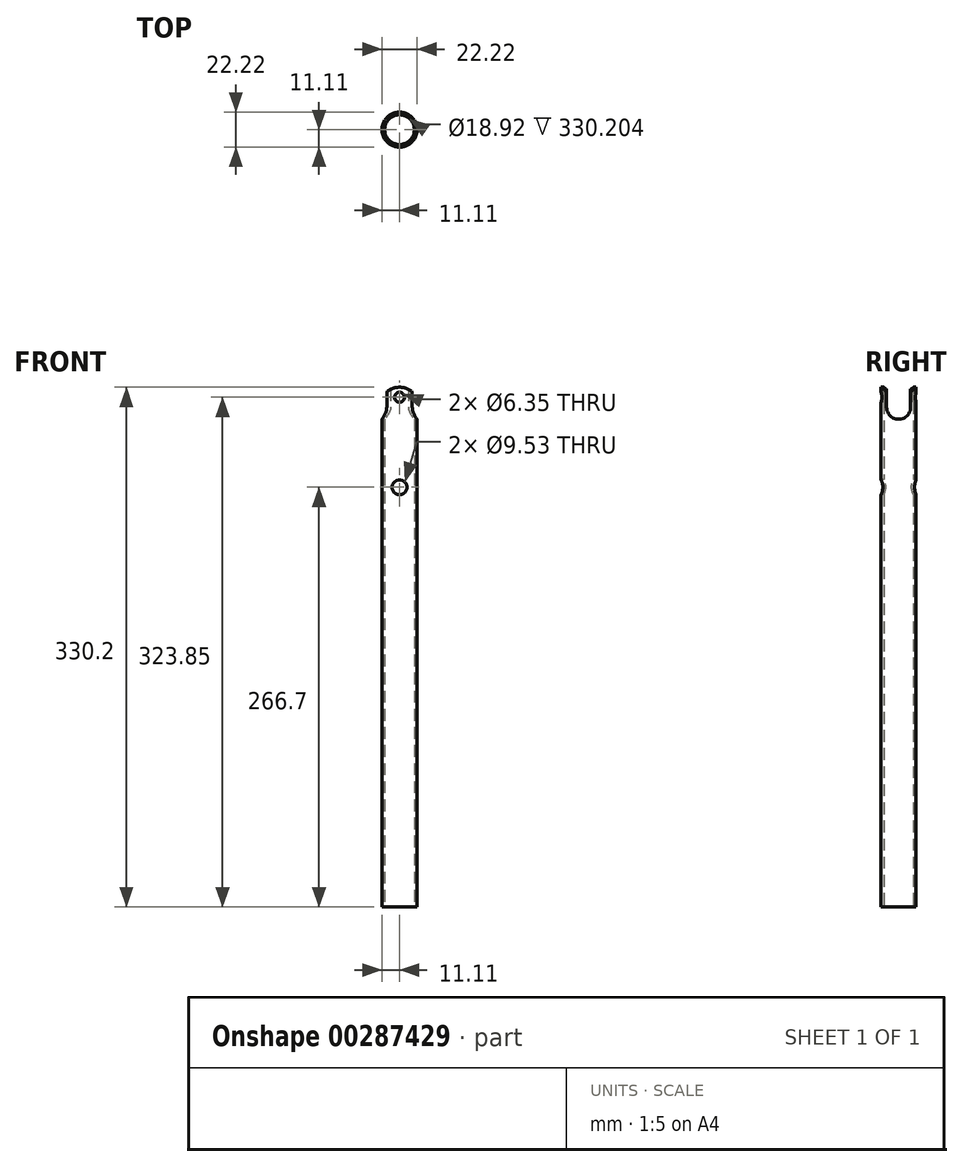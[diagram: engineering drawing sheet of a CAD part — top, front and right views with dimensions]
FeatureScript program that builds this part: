
annotation { "Feature Type Name" : "Feature", "Feature Type Description" : "" }
export const myFeature = defineFeature(function(context is Context, id is Id, definition is map)
    precondition{}
    {
        {
            var Q0;
            Q0=qCreatedBy(makeId("Top.planeOp"),FACE);
            var sketch = newSketch(context, id + "F0", { "sketchPlane" : qUnion([Q0])});
            skCircle(sketch, "E0", {"center": v(0, 0) * mm, "radius": 11.11 * mm});
            skCircle(sketch, "E1", {"center": v(0, 0) * mm, "radius": 9.46 * mm});
            skSolve(sketch);
        }
        {
            var Q0;
            Q0=makeQuery(id+"F0.imprint","IMPRINT",FACE,{"disambiguationData":[TD([[makeQuery(id+"F0.imprint","IMPRINT",EDGE,{"derivedFrom":sQuery(id+"F0.wireOp",EDGE,"E0")}),1.0]])]});
            var Q1;
            Q1=sQuery(id+"F0.wireOp",EDGE,"E0");
            extrude(context, id + "F1", {"entities" : qUnion([Q0]), "surfaceEntities" : qUnion([Q1]), "depth" : 228.6 * mm});
        }
        {
            var Q0;
            Q0=qCreatedBy(makeId("Front.planeOp"),FACE);
            var sketch = newSketch(context, id + "F2", { "sketchPlane" : qUnion([Q0])});
            skCircle(sketch, "E2", {"center": v(0, 228.6) * mm, "radius": 12.7 * mm});
            skPoint(sketch, "E3", {"position": v(12.7, 228.6) * mm});
            skPoint(sketch, "E4", {"position": v(-12.7, 228.6) * mm});
            skLineSegment(sketch, "E5", {"start": v(-12.7, 228.6) * mm, "end": v(12.7, 228.6) * mm});
            skCircle(sketch, "E6", {"center": v(0, 234.95) * mm, "radius": 3.18 * mm});
            skSolve(sketch);
        }
        {
            var Q0;
            {var subQ0=sQuery(id+"F2.wireOp",EDGE,"E5");Q0=makeQuery(id+"F2.imprint","IMPRINT",FACE,{"disambiguationData":[TD([[makeQuery(id+"F2.imprint","IMPRINT",EDGE,{"derivedFrom":subQ0}),1.0]])]});}
            extrude(context, id + "F3", {"entities" : qUnion([Q0]), "operationType" : NewBodyOperationType.ADD, "oppositeDirection" : true, "depth" : 12.7 * mm});
        }
        {
            var Q0;
            Q0=makeQuery(id+"F3.opExtrude","CAP_FACE",FACE,{"disambiguationData":[OSD([sQuery(id+"F2.wireOp",EDGE,"E2"),sQuery(id+"F2.wireOp",EDGE,"E5")])],"isStart":true});
            extrude(context, id + "F4", {"entities" : qUnion([Q0]), "operationType" : NewBodyOperationType.ADD, "depth" : 12.7 * mm});
        }
        {
            var Q0;
            Q0=makeQuery(id+"F4.boolean.opBoolean","SPLIT",FACE,{"disambiguationData":[OD(1.0)],"derivedFrom":makeQuery(id+"F4.opExtrude","SWEPT_FACE",FACE,{"disambiguationData":[OSD([sQuery(id+"F2.wireOp",EDGE,"E5")])]})});
            var Q1;
            {var subQ0=sQuery(id+"F2.wireOp",EDGE,"E5");var subQ1=sQuery(id+"F2.wireOp",EDGE,"E2");var subQ2=sQuery(id+"F0.wireOp",EDGE,"E0");var subQ3=makeQuery(id+"F3.opExtrude","SWEPT_FACE",FACE,{"disambiguationData":[OSD([subQ0])]});Q1=makeQuery(id+"F3.boolean.opBoolean","SPLIT",FACE,{"disambiguationData":[TD([makeQuery(id+"F1.opExtrude","SWEPT_FACE",FACE,{"disambiguationData":[OSD([subQ2])]}),makeQuery(id+"F1.opExtrude","CAP_FACE",FACE,{"disambiguationData":[OSD([subQ2,sQuery(id+"F0.wireOp",EDGE,"E1")])],"isStart":false}),makeQuery(id+"F3.opExtrude","SWEPT_FACE",FACE,{"disambiguationData":[OSD([subQ1])]}),makeQuery(id+"F3.opExtrude","CAP_FACE",FACE,{"disambiguationData":[OSD([subQ1,subQ0])],"isStart":true}),makeQuery(id+"F3.opExtrude","CAP_FACE",FACE,{"disambiguationData":[OSD([subQ1,subQ0])],"isStart":false}),subQ3]),OD(1.0)],"derivedFrom":subQ3});}
            var Q2;
            {var subQ0=sQuery(id+"F2.wireOp",EDGE,"E5");var subQ1=sQuery(id+"F2.wireOp",EDGE,"E2");var subQ2=sQuery(id+"F0.wireOp",EDGE,"E0");var subQ3=makeQuery(id+"F3.opExtrude","SWEPT_FACE",FACE,{"disambiguationData":[OSD([subQ0])]});Q2=makeQuery(id+"F3.boolean.opBoolean","SPLIT",FACE,{"disambiguationData":[TD([makeQuery(id+"F1.opExtrude","SWEPT_FACE",FACE,{"disambiguationData":[OSD([subQ2])]}),makeQuery(id+"F1.opExtrude","CAP_FACE",FACE,{"disambiguationData":[OSD([subQ2,sQuery(id+"F0.wireOp",EDGE,"E1")])],"isStart":false}),makeQuery(id+"F3.opExtrude","SWEPT_FACE",FACE,{"disambiguationData":[OSD([subQ1])]}),makeQuery(id+"F3.opExtrude","CAP_FACE",FACE,{"disambiguationData":[OSD([subQ1,subQ0])],"isStart":true}),makeQuery(id+"F3.opExtrude","CAP_FACE",FACE,{"disambiguationData":[OSD([subQ1,subQ0])],"isStart":false}),subQ3]),OD(0.0)],"derivedFrom":subQ3});}
            var Q3;
            Q3=makeQuery(id+"F4.boolean.opBoolean","SPLIT",FACE,{"disambiguationData":[OD(0.0)],"derivedFrom":makeQuery(id+"F4.opExtrude","SWEPT_FACE",FACE,{"disambiguationData":[OSD([sQuery(id+"F2.wireOp",EDGE,"E5")])]})});
            extrude(context, id + "F5", {"entities" : qUnion([Q0, Q1, Q2, Q3]), "operationType" : NewBodyOperationType.REMOVE, "oppositeDirection" : true, "depth" : 25.4 * mm});
        }
        {
            var Q0;
            Q0=qCreatedBy(makeId("Right.planeOp"),FACE);
            var sketch = newSketch(context, id + "F6", { "sketchPlane" : qUnion([Q0])});
            skLineSegment(sketch, "E7", {"start": v(0, 228.6) * mm, "end": v(-7.62, 228.6) * mm});
            skLineSegment(sketch, "E8", {"start": v(0, 228.6) * mm, "end": v(7.62, 228.6) * mm});
            skLineSegment(sketch, "E9", {"start": v(0, 234.75) * mm, "end": v(0, 234.75) * mm});
            skCircle(sketch, "E10", {"center": v(0, 228.6) * mm, "radius": 7.62 * mm});
            skLineSegment(sketch, "E11", {"start": v(7.62, 228.6) * mm, "end": v(7.62, 246.2) * mm});
            skLineSegment(sketch, "E12", {"start": v(-7.62, 228.6) * mm, "end": v(-7.62, 246.2) * mm});
            skLineSegment(sketch, "E13", {"start": v(-7.62, 246.2) * mm, "end": v(7.62, 246.2) * mm});
            skSolve(sketch);
        }
        {
            var Q0;
            Q0=qSketchRegion(id+"F6",true);
            extrude(context, id + "F7", {"entities" : qUnion([Q0]), "operationType" : NewBodyOperationType.REMOVE, "oppositeDirection" : true, "depth" : 12.7 * mm});
        }
        {
            var Q0;
            Q0=qSketchRegion(id+"F6",true);
            extrude(context, id + "F8", {"entities" : qUnion([Q0]), "operationType" : NewBodyOperationType.REMOVE, "depth" : 12.7 * mm});
        }
        {
            var Q0;
            Q0=makeQuery(id+"F0.imprint","IMPRINT",FACE,{"disambiguationData":[TD([[makeQuery(id+"F0.imprint","IMPRINT",EDGE,{"derivedFrom":sQuery(id+"F0.wireOp",EDGE,"E0")}),1.0]])]});
            var sketch = newSketch(context, id + "F9", { "sketchPlane" : qUnion([Q0])});
            skCircle(sketch, "E14", {"center": v(0, 0) * mm, "radius": 11.11 * mm});
            skCircle(sketch, "E15", {"center": v(0, 0) * mm, "radius": 9.46 * mm});
            skSolve(sketch);
        }
        {
            var Q0;
            Q0=qSketchRegion(id+"F9",true);
            extrude(context, id + "F10", {"entities" : qUnion([Q0]), "operationType" : NewBodyOperationType.ADD, "oppositeDirection" : true, "depth" : 88.9 * mm});
        }
        {
            var Q0;
            Q0=qCreatedBy(makeId("Top.planeOp"),FACE);
            cPlane(context, id + "F11", {"entities" : qUnion([Q0]), "cplaneType" : CPlaneType.OFFSET, "offset" : 177.8 * mm, "width" : 152.4 * mm, "height" : 152.4 * mm});
        }
        {
            var Q0;
            Q0=qCreatedBy(makeId("Front.planeOp"),FACE);
            var sketch = newSketch(context, id + "F12", { "sketchPlane" : qUnion([Q0])});
            skCircle(sketch, "E16", {"center": v(0, 177.8) * mm, "radius": 4.76 * mm});
            skLineSegment(sketch, "E17", {"start": v(0, 177.8) * mm, "end": v(0, -88.9) * mm});
            skSolve(sketch);
        }
        {
            var Q0;
            Q0=qSketchRegion(id+"F12",true);
            extrude(context, id + "F13", {"entities" : qUnion([Q0]), "operationType" : NewBodyOperationType.REMOVE, "oppositeDirection" : true, "depth" : 50.8 * mm, "symmetric" : true});
        }
        {
            var Q0;
            Q0=qCreatedBy(id+"F11.planeOp",FACE);
            var sketch = newSketch(context, id + "F14", { "sketchPlane" : qUnion([Q0])});
            skCircle(sketch, "E18", {"center": v(0, 0) * mm, "radius": 9.46 * mm});
            skSolve(sketch);
        }
        {
            var Q0;
            Q0=qSketchRegion(id+"F14",true);
            extrude(context, id + "F15", {"entities" : qUnion([Q0]), "operationType" : NewBodyOperationType.REMOVE, "depth" : 87.88 * mm});
        }
    });
